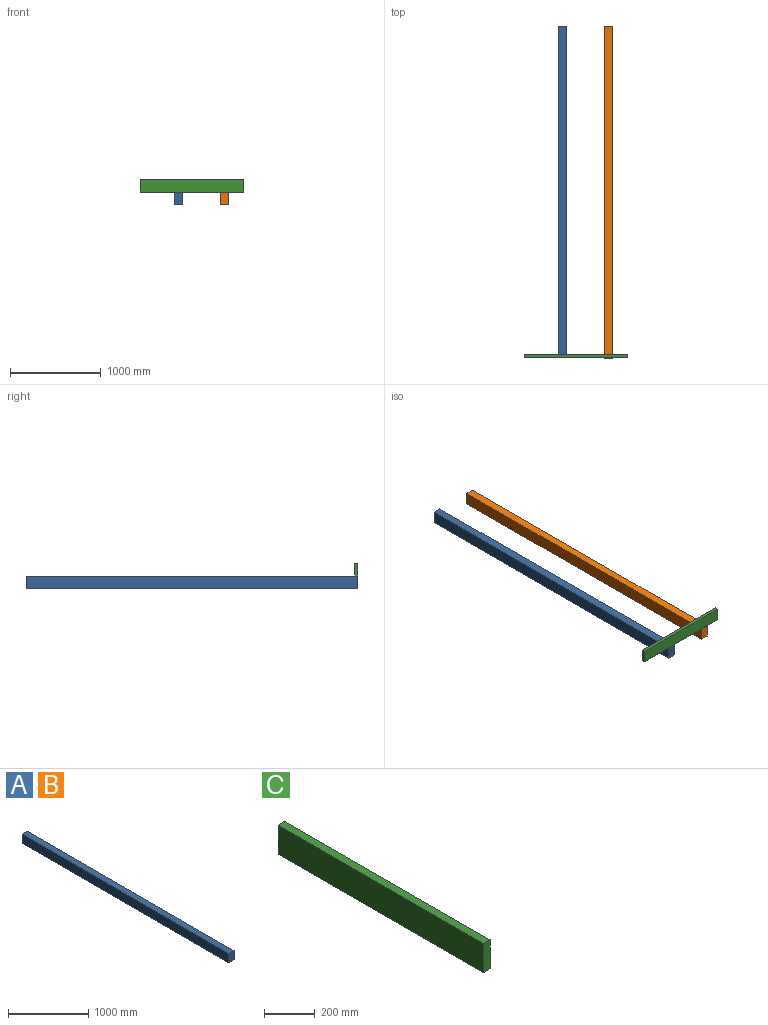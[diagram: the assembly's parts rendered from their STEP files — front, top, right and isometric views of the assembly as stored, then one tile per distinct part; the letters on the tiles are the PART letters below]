
ASSEMBLY  parts=3 mates=3
PART A: 6 faces, bbox 88.9x3657.6x139.7 mm
  f0: plane 3657.6x139.7mm, normal (-1,0,0), area 510966.7mm2, adj f1,f3,f4,f5
  f1: plane 3657.6x88.9mm, normal (0,0,-1), area 325160.6mm2, adj f0,f2,f4,f5
  f2: plane 3657.6x139.7mm, normal (1,0,0), area 510966.7mm2, adj f1,f3,f4,f5
  f3: plane 3657.6x88.9mm, normal (0,0,1), area 325160.6mm2, adj f0,f2,f4,f5
  f4: plane 139.7x88.9mm, normal (0,-1,0), area 12419.3mm2, adj f0,f1,f2,f3
  f5: plane 139.7x88.9mm, normal (0,1,0), area 12419.3mm2, adj f0,f1,f2,f3
PART B: same geometry as A
PART C: 6 faces, bbox 38.1x1143x139.7 mm
  f0: plane 1143x139.7mm, normal (-1,0,0), area 159677.1mm2, adj f1,f3,f4,f5
  f1: plane 1143x38.1mm, normal (0,0,-1), area 43548.3mm2, adj f0,f2,f4,f5
  f2: plane 1143x139.7mm, normal (1,0,0), area 159677.1mm2, adj f1,f3,f4,f5
  f3: plane 1143x38.1mm, normal (0,0,1), area 43548.3mm2, adj f0,f2,f4,f5
  f4: plane 139.7x38.1mm, normal (0,-1,0), area 5322.6mm2, adj f0,f1,f2,f3
  f5: plane 139.7x38.1mm, normal (0,1,0), area 5322.6mm2, adj f0,f1,f2,f3
PLACE A rot(axis=(0,-0.05,1),0deg) t=(-809.06,-156.44,-81.96)mm
PLACE B t=(-301.06,-156.44,-81.96)mm fixed
PLACE C rot(axis=(0,0,-1),90deg) t=(-46.75,-3775.94,57.74)mm
MATE planar C.f2 <-> B.f4  axis (0,-1,0) through (-618.25,-3814.04,127.59)mm
MATE planar B.f3 <-> A.f3  axis (0,0,1) through (-256.61,-1985.24,57.74)mm
MATE planar C.f1 <-> A.f3  axis (0,0,-1) through (-618.25,-3775.94,57.74)mm
